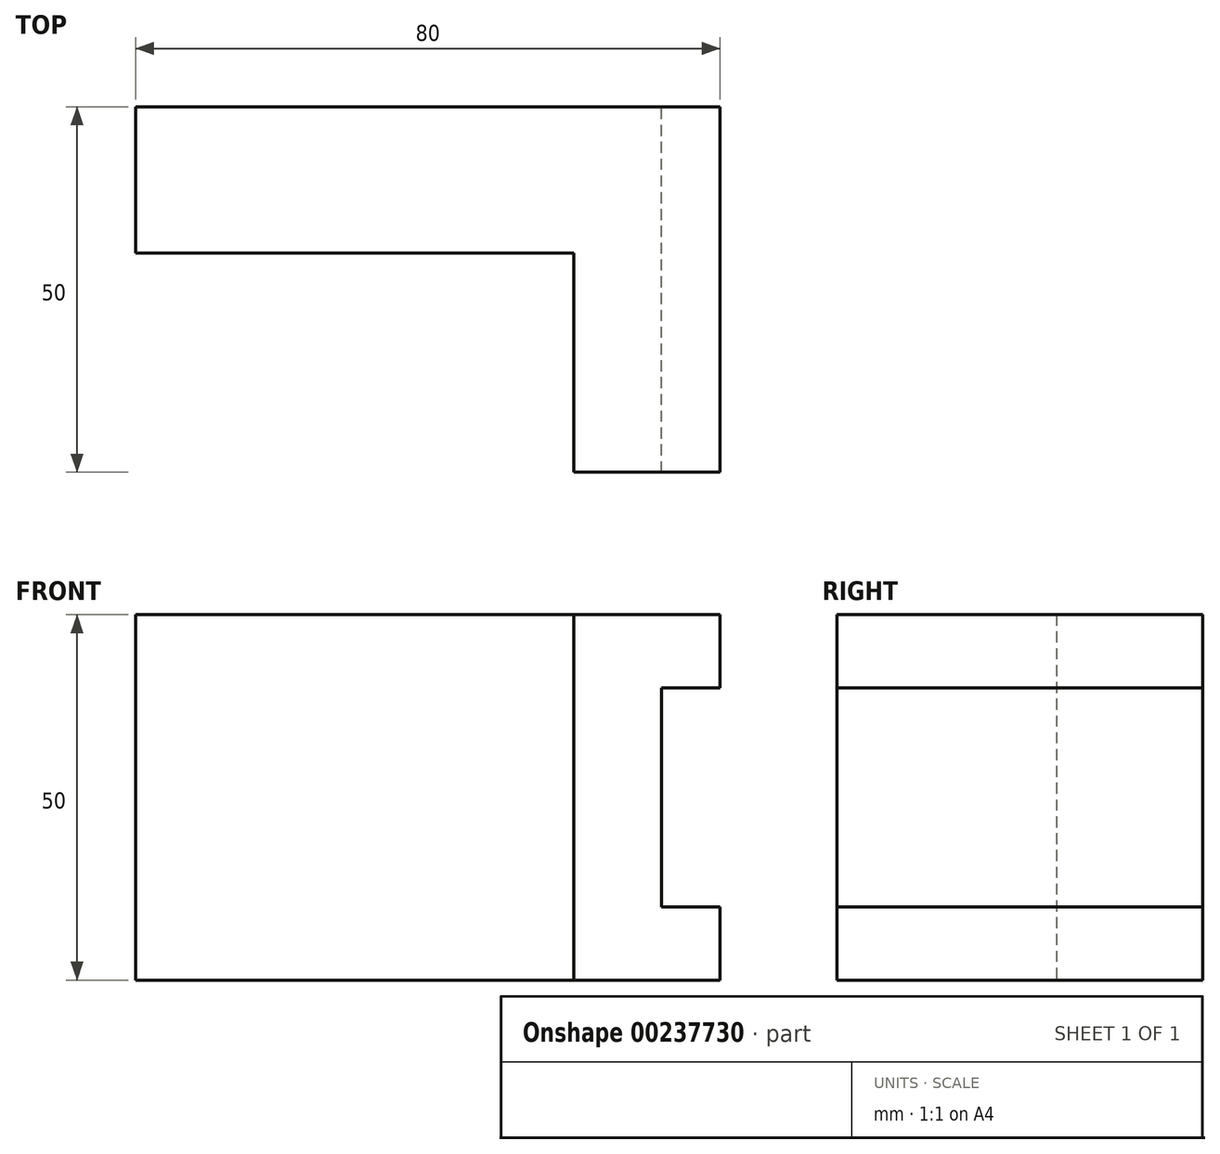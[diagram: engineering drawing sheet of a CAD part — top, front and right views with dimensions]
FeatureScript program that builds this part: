
annotation { "Feature Type Name" : "Feature", "Feature Type Description" : "" }
export const myFeature = defineFeature(function(context is Context, id is Id, definition is map)
    precondition{}
    {
        {
            var Q0;
            Q0=qCreatedBy(makeId("Front.planeOp"),FACE);
            var sketch = newSketch(context, id + "F0", { "sketchPlane" : qUnion([Q0])});
            skLineSegment(sketch, "E0.bottom", {"start": v(-61.12, 37.07) * mm, "end": v(-1.12, 37.07) * mm});
            skLineSegment(sketch, "E0.top", {"start": v(-61.12, -12.93) * mm, "end": v(-1.12, -12.93) * mm});
            skLineSegment(sketch, "E0.left", {"start": v(-61.12, 37.07) * mm, "end": v(-61.12, -12.93) * mm});
            skLineSegment(sketch, "E0.right", {"start": v(-1.12, 37.07) * mm, "end": v(-1.12, -12.93) * mm});
            skLineSegment(sketch, "E1.bottom", {"start": v(-1.12, 37.07) * mm, "end": v(18.88, 37.07) * mm});
            skLineSegment(sketch, "E1.top", {"start": v(-1.12, -12.93) * mm, "end": v(18.88, -12.93) * mm});
            skLineSegment(sketch, "E1.right", {"start": v(18.88, 37.07) * mm, "end": v(18.88, -12.93) * mm});
            skLineSegment(sketch, "E2.bottom", {"start": v(18.88, 27.07) * mm, "end": v(10.88, 27.07) * mm});
            skLineSegment(sketch, "E2.top", {"start": v(18.88, -2.93) * mm, "end": v(10.88, -2.93) * mm});
            skLineSegment(sketch, "E2.left", {"start": v(18.88, 27.07) * mm, "end": v(18.88, -2.93) * mm});
            skLineSegment(sketch, "E2.right", {"start": v(10.88, 27.07) * mm, "end": v(10.88, -2.93) * mm});
            skSolve(sketch);
        }
        {
            var Q0;
            Q0=makeQuery(id+"F0.imprint","IMPRINT",FACE,{"disambiguationData":[TD([[makeQuery(id+"F0.imprint","IMPRINT",EDGE,{"derivedFrom":sQuery(id+"F0.wireOp",EDGE,"E0.bottom")}),-1.0]])]});
            extrude(context, id + "F1", {"entities" : qUnion([Q0]), "depth" : 20 * mm});
        }
        {
            var Q0;
            {var subQ1=sQuery(id+"F0.wireOp",EDGE,"E1.bottom");Q0=makeQuery(id+"F0.imprint","IMPRINT",FACE,{"disambiguationData":[TD([[makeQuery(id+"F0.imprint","IMPRINT",EDGE,{"derivedFrom":subQ1}),-1.0]])]});}
            extrude(context, id + "F2", {"entities" : qUnion([Q0]), "operationType" : NewBodyOperationType.ADD, "depth" : 50 * mm});
        }
    });
